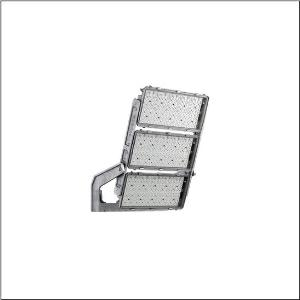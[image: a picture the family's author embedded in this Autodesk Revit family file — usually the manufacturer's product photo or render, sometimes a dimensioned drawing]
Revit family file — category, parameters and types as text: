
# Revit family: floodlight_fl_11_maxi_pro_remote___pl64blc_5xa779426w01aa_c02a
name_source: partatom
category: Lighting Fixtures
units: mm (PartAtom-declared; Revit-internal decimal feet)

## family parameters
Cut with Voids When Loaded = No
Host = Face
Light Source = No
Part Type = Normal
Room Calculation Point = No
Round Connector Dimension = Use Diameter
Shared = No

## types (1)
- --- (1 x LED, 140990 lm, 1516.9 W, 4000K)
    Apparent Load = 1517 VA
    CIE Flux Codes = 28 83 99 100 100
    Color Rendering = 70
    Color Temperature = 4000K
    Default Elevation = 1800 mm
    Description = Floodlight FL 11  maxi  pro Remote floodlight; light control with lens of PMMA; cover panel of toughened safety glass, transparent; light distribution: PL64BLC, asymmetric direct distribution, LEDcolour temperature: 4000K, rated luminous flux: 140.990lm, colour rendering: CRI > 70, light colour: 740; luminous efficacy: 93lm/W; brightness control: DALI 2 (1 DALI address); with terminal, 8-pole, max. 2.5mm², mains connection: 220..240V/380..400V AC, 50/60Hz, surge voltage resistance: line to ground: 10kV, ECG replaceable separately, no afterglow with DALI off / DMX off command, LED unit replaceable without ESD environment, dustproof LED module, dimming range 10..100%; 1517W floodlight with 2x LED unit of diecast aluminium, coated grey; length: 713mm / width: 651mm / height: 338mm; mounting bracket, of diecast aluminium, uncoated, natural, equipment: Power, protection rating (complete): IP66; insulation class (complete): insulation class I (protective earthing); certification: CE, ENEC, VDE; ball protection: ball impact resistance with accessories, impact resistance: IK07; only for outdoor installations, rated ambient temperature 10°C, permissible operating ambient temperature: -40..+30°C, permissible storage temperature: -40..+85°C; packaging unit: 1 piece

Light Distribution: PL64BLC
    Height = 320 mm
    Lamp = 1 x LED
    Lamp Light Flux = 140990 lm
    Lamp Power = 1516.9 W
    Lamp count = 1
    Length = 1002 mm
    Luminous efficacy = 93 lm/W
    Manufacturer = Siteco
    ModVariant = No
    Model = 5XA779426W01AA
    Mounting Place = Ceiling
    Mounting Type = Surface mounted
    Number of Poles = 1
    OnlyDefault = Yes
    Power Factor = 1
    Product Name = Floodlight FL 11 maxi pro Remote | PL64BLC
    Product group = floodlight | ceiling mounted
    ProductGroupID = 303
    Protection Class = Protection class I
    Protection Degree = IP 66
    RLX_Detail_Level = 1
    RLX_Emergency_Light_Flux = 0 lm
    RLX_Emergency_Type = 0
    RLX_Emergency_Type_DB = No
    RlxData = <blob elided: 52493 chars, md5=258684f2>
    Socket = socket
    Standby Power = 0 W
    System Light Flux = 140990 lm
    System Power = 1517 W
    Type Comments = factory setting: luminous flux: 100 % | dim-lin: 254 | 1070 mA
    Type Image = l_1006784.jpg
    URL = http://relux.com
    VarID = @adj_033129
    Voltage = 0 V
    Weight = 0.00 kg
    Width = 655 mm

## geometry (parser evidence)
native form markers: Blend x4, Sweep x13
no freeform markers — native parametric forms only
